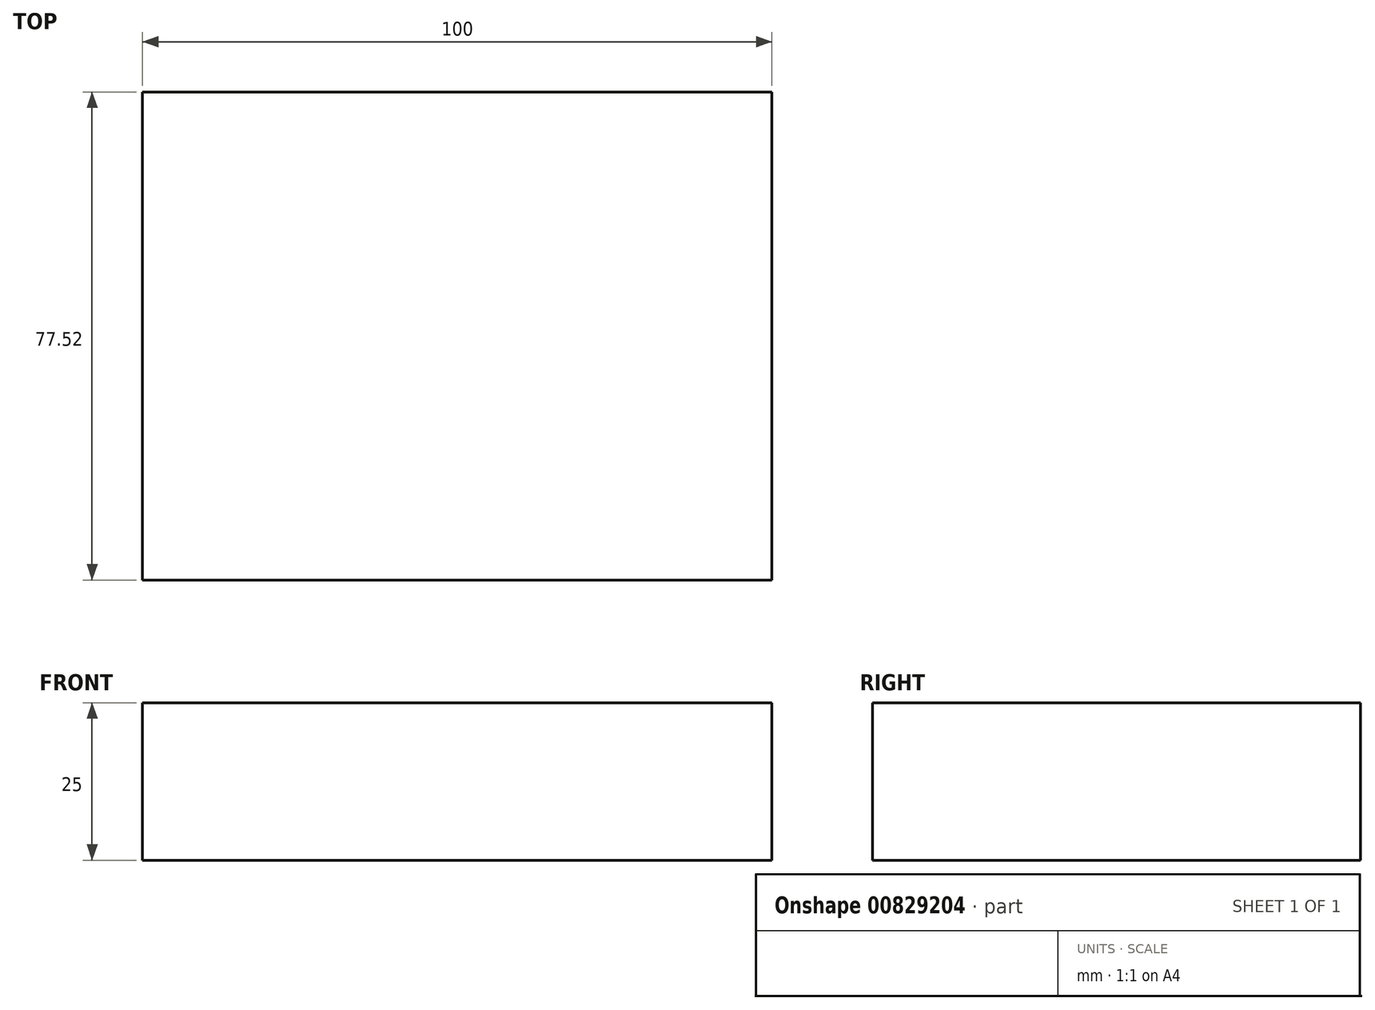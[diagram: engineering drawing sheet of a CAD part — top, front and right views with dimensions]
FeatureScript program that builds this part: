
annotation { "Feature Type Name" : "Feature", "Feature Type Description" : "" }
export const myFeature = defineFeature(function(context is Context, id is Id, definition is map)
    precondition{}
    {
        {
            var Q0;
            Q0=qCreatedBy(makeId("Top.planeOp"),FACE);
            var sketch = newSketch(context, id + "F0", { "sketchPlane" : qUnion([Q0])});
            skLineSegment(sketch, "E0.bottom", {"start": v(50, -38.76) * mm, "end": v(-50, -38.76) * mm});
            skLineSegment(sketch, "E0.top", {"start": v(50, 38.76) * mm, "end": v(-50, 38.76) * mm});
            skLineSegment(sketch, "E0.left", {"start": v(50, -38.76) * mm, "end": v(50, 38.76) * mm});
            skLineSegment(sketch, "E0.right", {"start": v(-50, -38.76) * mm, "end": v(-50, 38.76) * mm});
            skPoint(sketch, "E0.middle", {"position": v(0, 0) * mm});
            skSolve(sketch);
        }
        {
            var Q0;
            Q0 = qSketchRegion(id + "F0", true);
            extrude(context, id + "F1", {"entities" : qUnion([Q0]), "depth" : 25 * mm, "offsetDistance" : 25 * mm});
        }
    });
